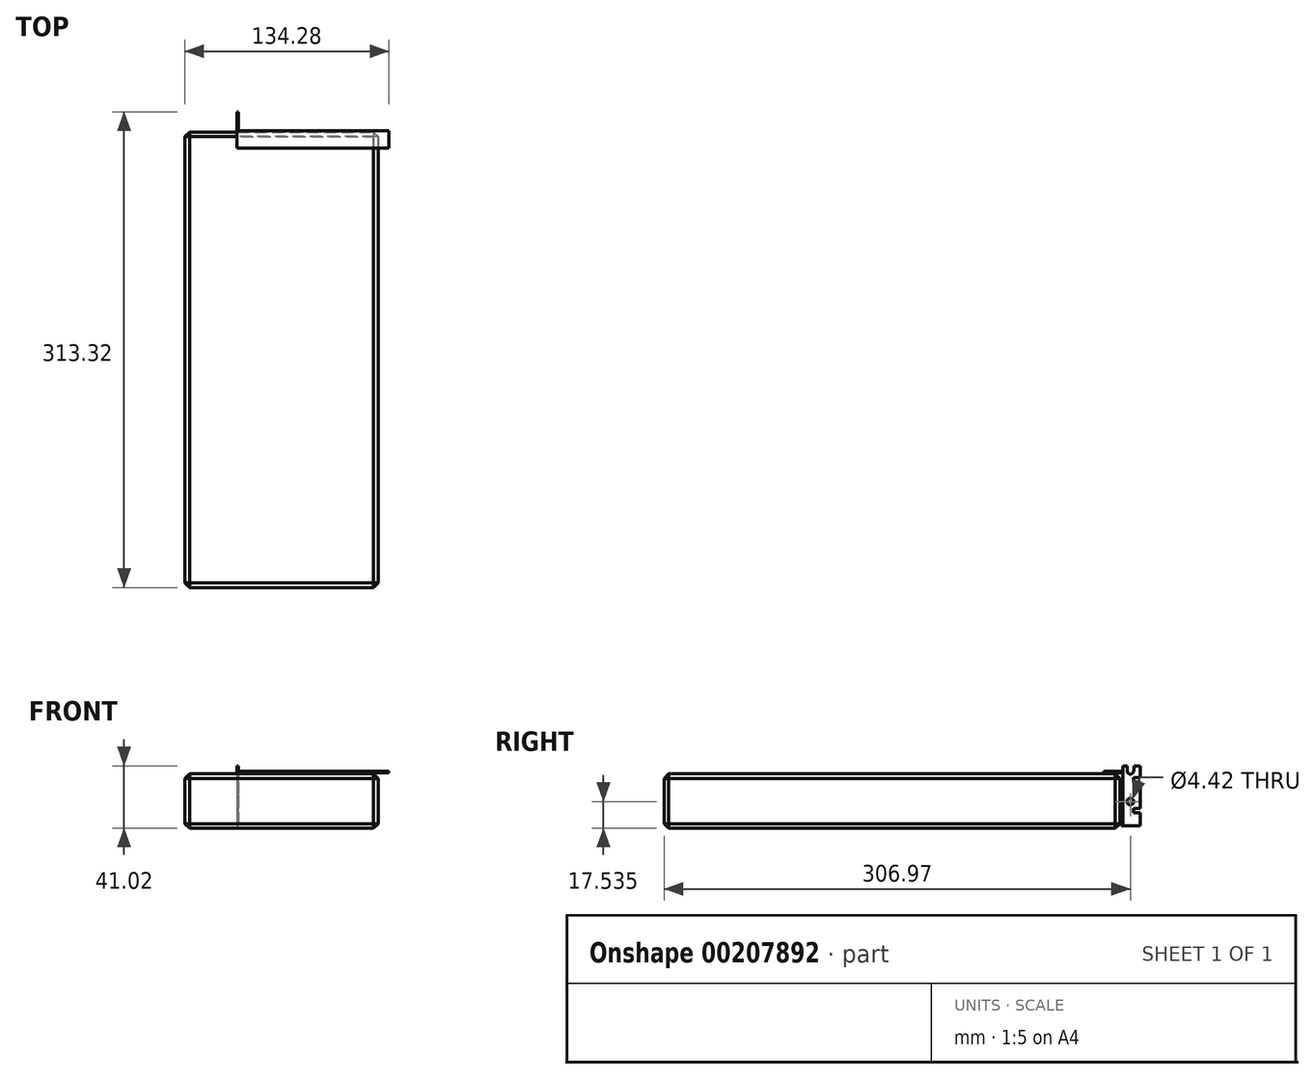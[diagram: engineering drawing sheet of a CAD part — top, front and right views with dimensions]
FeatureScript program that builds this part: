
annotation { "Feature Type Name" : "Feature", "Feature Type Description" : "" }
export const myFeature = defineFeature(function(context is Context, id is Id, definition is map)
    precondition{}
    {
        {
            var Q0;
            Q0=qCreatedBy(makeId("Top.planeOp"),FACE);
            var sketch = newSketch(context, id + "F0", { "sketchPlane" : qUnion([Q0])});
            skLineSegment(sketch, "E0.bottom", {"start": v(-143.4, -242.84) * mm, "end": v(-114.55, -242.84) * mm});
            skLineSegment(sketch, "E0.top", {"start": v(-143.4, 57.16) * mm, "end": v(-114.55, 57.16) * mm});
            skLineSegment(sketch, "E0.left", {"start": v(-143.4, -242.84) * mm, "end": v(-143.4, 57.16) * mm});
            skLineSegment(sketch, "E0.right", {"start": v(-114.55, -242.84) * mm, "end": v(-114.55, 57.16) * mm});
            skPoint(sketch, "E1", {"position": v(-3.4, -242.84) * mm});
            skLineSegment(sketch, "E2", {"start": v(11.76, 58.2) * mm, "end": v(11.76, 59.05) * mm});
            skLineSegment(sketch, "E3", {"start": v(11.76, 59.05) * mm, "end": v(-108.26, 59.05) * mm});
            skLineSegment(sketch, "E4", {"start": v(-108.26, 59.05) * mm, "end": v(-108.26, 70.48) * mm});
            skLineSegment(sketch, "E5", {"start": v(-108.26, 70.48) * mm, "end": v(-109.12, 70.48) * mm});
            skLineSegment(sketch, "E6.bottom", {"start": v(-114.55, -242.84) * mm, "end": v(-16.15, -242.84) * mm});
            skLineSegment(sketch, "E6.top", {"start": v(-114.55, 57.16) * mm, "end": v(-16.15, 57.16) * mm});
            skLineSegment(sketch, "E6.right", {"start": v(-16.15, -242.84) * mm, "end": v(-16.15, 57.16) * mm});
            skLineSegment(sketch, "E7.bottom", {"start": v(-16.15, 57.16) * mm, "end": v(-7.9, 57.16) * mm});
            skLineSegment(sketch, "E7.top", {"start": v(-16.15, 42.16) * mm, "end": v(-7.9, 42.16) * mm});
            skLineSegment(sketch, "E7.left", {"start": v(-16.15, 57.16) * mm, "end": v(-16.15, 42.16) * mm});
            skLineSegment(sketch, "E7.right", {"start": v(-7.9, 57.16) * mm, "end": v(-7.9, 42.16) * mm});
            skPoint(sketch, "E8", {"position": v(-7.9, -242.84) * mm});
            skLineSegment(sketch, "E9.bottom", {"start": v(-16.15, 23.8) * mm, "end": v(-7.9, 23.8) * mm});
            skLineSegment(sketch, "E9.top", {"start": v(-16.15, 15.8) * mm, "end": v(-7.9, 15.8) * mm});
            skLineSegment(sketch, "E9.left", {"start": v(-16.15, 23.8) * mm, "end": v(-16.15, 15.8) * mm});
            skLineSegment(sketch, "E9.right", {"start": v(-7.9, 23.8) * mm, "end": v(-7.9, 15.8) * mm});
            skPoint(sketch, "E10", {"position": v(-3.4, 57.16) * mm});
            skLineSegment(sketch, "E11", {"start": v(-16.15, 12.15) * mm, "end": v(-3.4, 12.15) * mm});
            skLineSegment(sketch, "E12", {"start": v(-3.4, 12.15) * mm, "end": v(-3.4, 0.95) * mm});
            skLineSegment(sketch, "E13", {"start": v(-3.4, 0.95) * mm, "end": v(-11.8, 0.95) * mm});
            skLineSegment(sketch, "E14", {"start": v(-11.8, 0.95) * mm, "end": v(-11.8, -0.95) * mm});
            skLineSegment(sketch, "E15", {"start": v(-11.8, -0.95) * mm, "end": v(-3.4, -0.95) * mm});
            skLineSegment(sketch, "E16", {"start": v(-3.4, -0.95) * mm, "end": v(-3.4, -72.15) * mm});
            skLineSegment(sketch, "E17", {"start": v(-3.4, -72.15) * mm, "end": v(-16.15, -72.15) * mm});
            skPoint(sketch, "E18", {"position": v(-11.8, 0) * mm});
            skArc(sketch, "E19", {"start": v(-14.32, 15.8) * mm, "mid": v(-16.15, 13.98) * mm, "end": v(-14.32, 12.15) * mm});
            skArc(sketch, "E20", {"start": v(-10.85, 0.95) * mm, "mid": v(-11.8, 0) * mm, "end": v(-10.85, -0.95) * mm});
            skLineSegment(sketch, "E21", {"start": v(-16.15, -81.9) * mm, "end": v(-11.35, -81.9) * mm});
            skLineSegment(sketch, "E22", {"start": v(-11.35, -81.9) * mm, "end": v(-11.35, -87.6) * mm});
            skLineSegment(sketch, "E23", {"start": v(-11.35, -87.6) * mm, "end": v(-8.77, -87.6) * mm});
            skLineSegment(sketch, "E24", {"start": v(-8.77, -87.6) * mm, "end": v(-6.35, -86.2) * mm});
            skLineSegment(sketch, "E25", {"start": v(-6.35, -86.2) * mm, "end": v(-6.35, -74.9) * mm});
            skLineSegment(sketch, "E26", {"start": v(-6.35, -74.9) * mm, "end": v(-12.38, -74.9) * mm});
            skLineSegment(sketch, "E27", {"start": v(-12.38, -74.9) * mm, "end": v(-12.38, -72.15) * mm});
            skArc(sketch, "E28", {"start": v(-11, -72.15) * mm, "mid": v(-12.38, -73.53) * mm, "end": v(-11, -74.9) * mm});
            skLineSegment(sketch, "E29", {"start": v(-108.26, 59.05) * mm, "end": v(-109.12, 59.05) * mm});
            skLineSegment(sketch, "E30", {"start": v(-109.12, 70.48) * mm, "end": v(-109.12, 59.05) * mm});
            skLineSegment(sketch, "E31", {"start": v(-109.12, 58.2) * mm, "end": v(-109.12, 59.05) * mm});
            skLineSegment(sketch, "E32", {"start": v(-108.26, 59.05) * mm, "end": v(-108.26, 58.2) * mm});
            skLineSegment(sketch, "E33", {"start": v(-108.26, 58.2) * mm, "end": v(-109.12, 58.2) * mm});
            skLineSegment(sketch, "E34", {"start": v(-108.26, 58.2) * mm, "end": v(11.76, 58.2) * mm});
            skPoint(sketch, "E35", {"position": v(0, 0) * mm});
            skPoint(sketch, "E36", {"position": v(0, 57.16) * mm});
            skSolve(sketch);
        }
        {
            var Q0;
            {var subQ7=sQuery(id+"F0.wireOp",EDGE,"E6.bottom");Q0=makeQuery(id+"F0.imprint","IMPRINT",FACE,{"disambiguationData":[TD([[makeQuery(id+"F0.imprint","IMPRINT",EDGE,{"derivedFrom":subQ7}),1.0]])]});}
            var Q1;
            Q1=makeQuery(id+"F0.imprint","IMPRINT",FACE,{"disambiguationData":[TD([[makeQuery(id+"F0.imprint","IMPRINT",EDGE,{"derivedFrom":sQuery(id+"F0.wireOp",EDGE,"E0.bottom")}),1.0]])]});
            var Q2;
            {var subQ5=sQuery(id+"F0.wireOp",EDGE,"E21");Q2=makeQuery(id+"F0.imprint","IMPRINT",FACE,{"disambiguationData":[TD([[makeQuery(id+"F0.imprint","IMPRINT",EDGE,{"derivedFrom":subQ5}),1.0]])]});}
            var Q3;
            {var subQ0=sQuery(id+"F0.wireOp",EDGE,"E27");var subQ1=sQuery(id+"F0.wireOp",EDGE,"E26");var subQ2=makeQuery(id+"F0.imprint","INTERSECT",VERTEX,{"derivedFrom":[subQ1,subQ0]});Q3=makeQuery(id+"F0.imprint","IMPRINT",FACE,{"disambiguationData":[TD([[makeQuery(id+"F0.imprint","IMPRINT",EDGE,{"disambiguationData":[TD([[subQ2,1.0]])],"derivedFrom":subQ1}),-1.0]])]});}
            var Q4;
            {var subQ0=sQuery(id+"F0.wireOp",EDGE,"E27");var subQ1=sQuery(id+"F0.wireOp",EDGE,"E17");var subQ2=makeQuery(id+"F0.imprint","INTERSECT",VERTEX,{"derivedFrom":[subQ1,subQ0]});Q4=makeQuery(id+"F0.imprint","IMPRINT",FACE,{"disambiguationData":[TD([[makeQuery(id+"F0.imprint","IMPRINT",EDGE,{"disambiguationData":[TD([[subQ2,1.0]])],"derivedFrom":subQ1}),1.0]])]});}
            var Q5;
            {var subQ0=sQuery(id+"F0.wireOp",EDGE,"E15");var subQ1=sQuery(id+"F0.wireOp",EDGE,"E14");var subQ2=makeQuery(id+"F0.imprint","INTERSECT",VERTEX,{"derivedFrom":[subQ1,subQ0]});Q5=makeQuery(id+"F0.imprint","IMPRINT",FACE,{"disambiguationData":[TD([[makeQuery(id+"F0.imprint","IMPRINT",EDGE,{"disambiguationData":[TD([[subQ2,1.0]])],"derivedFrom":subQ1}),1.0]])]});}
            var Q6;
            {var subQ0=sQuery(id+"F0.wireOp",EDGE,"E14");var subQ1=sQuery(id+"F0.wireOp",EDGE,"E13");var subQ2=makeQuery(id+"F0.imprint","INTERSECT",VERTEX,{"derivedFrom":[subQ1,subQ0]});Q6=makeQuery(id+"F0.imprint","IMPRINT",FACE,{"disambiguationData":[TD([[makeQuery(id+"F0.imprint","IMPRINT",EDGE,{"disambiguationData":[TD([[subQ2,1.0]])],"derivedFrom":subQ1}),1.0]])]});}
            var Q7;
            {var subQ7=sQuery(id+"F0.wireOp",EDGE,"E12");Q7=makeQuery(id+"F0.imprint","IMPRINT",FACE,{"disambiguationData":[TD([[makeQuery(id+"F0.imprint","IMPRINT",EDGE,{"derivedFrom":subQ7}),-1.0]])]});}
            var Q8;
            {var subQ0=sQuery(id+"F0.wireOp",EDGE,"E11");var subQ1=sQuery(id+"F0.wireOp",EDGE,"E6.right");var subQ2=makeQuery(id+"F0.imprint","INTERSECT",VERTEX,{"derivedFrom":[subQ1,subQ0]});Q8=makeQuery(id+"F0.imprint","IMPRINT",FACE,{"disambiguationData":[TD([[makeQuery(id+"F0.imprint","IMPRINT",EDGE,{"disambiguationData":[TD([[subQ2,-1.0]])],"derivedFrom":subQ1}),-1.0]])]});}
            var Q9;
            {var subQ0=sQuery(id+"F0.wireOp",EDGE,"E9.top");var subQ3=sQuery(id+"F0.wireOp",EDGE,"E19");var subQ5=makeQuery(id+"F0.imprint","INTERSECT",VERTEX,{"derivedFrom":[subQ0,subQ3]});Q9=makeQuery(id+"F0.imprint","IMPRINT",FACE,{"disambiguationData":[TD([[makeQuery(id+"F0.imprint","IMPRINT",EDGE,{"disambiguationData":[TD([[subQ5,-1.0]])],"derivedFrom":subQ3}),-1.0]])]});}
            var Q10;
            Q10=makeQuery(id+"F0.imprint","IMPRINT",FACE,{"disambiguationData":[TD([[makeQuery(id+"F0.imprint","IMPRINT",EDGE,{"derivedFrom":sQuery(id+"F0.wireOp",EDGE,"E9.bottom")}),-1.0]])]});
            var Q11;
            Q11=makeQuery(id+"F0.imprint","IMPRINT",FACE,{"disambiguationData":[TD([[makeQuery(id+"F0.imprint","IMPRINT",EDGE,{"derivedFrom":sQuery(id+"F0.wireOp",EDGE,"E7.bottom")}),-1.0]])]});
            extrude(context, id + "F1", {"entities" : qUnion([Q0, Q1, Q2, Q3, Q4, Q5, Q6, Q7, Q8, Q9, Q10, Q11]), "endBound" : BoundingType.SYMMETRIC, "depth" : 1.57 * mm});
        }
        {
            var Q0;
            Q0=makeQuery(id+"F0.imprint","IMPRINT",FACE,{"disambiguationData":[TD([[makeQuery(id+"F0.imprint","IMPRINT",EDGE,{"derivedFrom":sQuery(id+"F0.wireOp",EDGE,"E2")}),1.0]])]});
            extrude(context, id + "F2", {"entities" : qUnion([Q0]), "depth" : 10 * mm, "hasSecondDirection" : true, "secondDirectionOppositeDirection" : true, "secondDirectionDepth" : 40 * mm});
        }
        {
            var Q0;
            Q0=makeQuery(id+"F2.opExtrude","SWEPT_FACE",FACE,{"disambiguationData":[OSD([sQuery(id+"F0.wireOp",EDGE,"E3")])]});
            var sketch = newSketch(context, id + "F3", { "sketchPlane" : qUnion([Q0])});
            skLineSegment(sketch, "E37", {"start": v(-4.49, -2.06) * mm, "end": v(-11.76, -2.06) * mm});
            skLineSegment(sketch, "E38", {"start": v(-11.76, -2.06) * mm, "end": v(-11.76, -12.25) * mm});
            skLineSegment(sketch, "E39", {"start": v(-11.76, -12.25) * mm, "end": v(-4.49, -12.25) * mm});
            skLineSegment(sketch, "E40", {"start": v(-4.49, -12.25) * mm, "end": v(-0.38, -16.37) * mm});
            skLineSegment(sketch, "E41", {"start": v(-0.38, -16.36) * mm, "end": v(101.78, -16.36) * mm});
            skLineSegment(sketch, "E42", {"start": v(108.26, -13.82) * mm, "end": v(108.26, 5.23) * mm});
            skLineSegment(sketch, "E43", {"start": v(108.26, 5.23) * mm, "end": v(105.34, 5.23) * mm});
            skLineSegment(sketch, "E44", {"start": v(103.7, 2.06) * mm, "end": v(-0.37, 2.05) * mm});
            skLineSegment(sketch, "E45", {"start": v(-0.37, 2.05) * mm, "end": v(-4.49, -2.06) * mm});
            skLineSegment(sketch, "E46.bottom", {"start": v(7.9, 0.79) * mm, "end": v(114.55, 0.79) * mm});
            skLineSegment(sketch, "E46.top", {"start": v(7.9, -0.78) * mm, "end": v(114.55, -0.78) * mm});
            skLineSegment(sketch, "E46.left", {"start": v(7.9, 0.78) * mm, "end": v(7.9, -0.78) * mm});
            skLineSegment(sketch, "E46.right", {"start": v(114.55, 0.79) * mm, "end": v(114.55, -0.78) * mm});
            skPoint(sketch, "E47", {"position": v(7.9, 0) * mm});
            skLineSegment(sketch, "E48", {"start": v(108.26, -13.82) * mm, "end": v(104.32, -13.82) * mm});
            skLineSegment(sketch, "E49", {"start": v(104.32, -13.82) * mm, "end": v(101.78, -16.36) * mm});
            skLineSegment(sketch, "E50", {"start": v(103.7, 2.05) * mm, "end": v(103.7, 3.59) * mm});
            skLineSegment(sketch, "E51", {"start": v(103.7, 3.59) * mm, "end": v(105.34, 5.23) * mm});
            skPoint(sketch, "E52", {"position": v(0, 0) * mm});
            skLineSegment(sketch, "E53", {"start": v(-11.76, -22.39) * mm, "end": v(-11.76, -32.58) * mm});
            skLineSegment(sketch, "E54", {"start": v(-11.76, -32.57) * mm, "end": v(-4.49, -32.57) * mm});
            skLineSegment(sketch, "E55", {"start": v(-4.49, -32.57) * mm, "end": v(-0.38, -36.69) * mm});
            skLineSegment(sketch, "E56", {"start": v(-0.38, -36.69) * mm, "end": v(101.78, -36.68) * mm});
            skLineSegment(sketch, "E57", {"start": v(104.32, -34.14) * mm, "end": v(101.78, -36.68) * mm});
            skLineSegment(sketch, "E58", {"start": v(104.32, -34.14) * mm, "end": v(108.26, -34.14) * mm});
            skLineSegment(sketch, "E59", {"start": v(108.26, -34.14) * mm, "end": v(108.26, -15.1) * mm});
            skLineSegment(sketch, "E60", {"start": v(108.26, -15.1) * mm, "end": v(105.34, -15.1) * mm});
            skLineSegment(sketch, "E61", {"start": v(105.34, -15.1) * mm, "end": v(103.7, -16.73) * mm});
            skLineSegment(sketch, "E62", {"start": v(103.7, -16.73) * mm, "end": v(103.7, -18.26) * mm});
            skLineSegment(sketch, "E63", {"start": v(103.7, -18.26) * mm, "end": v(-0.37, -18.27) * mm});
            skLineSegment(sketch, "E64", {"start": v(-11.76, -22.39) * mm, "end": v(-4.49, -22.39) * mm});
            skLineSegment(sketch, "E65", {"start": v(-4.49, -22.39) * mm, "end": v(-0.37, -18.27) * mm});
            skLineSegment(sketch, "E66", {"start": v(-0.38, -16.37) * mm, "end": v(-0.37, -18.27) * mm});
            skLineSegment(sketch, "E67", {"start": v(108.26, -13.82) * mm, "end": v(108.26, -15.1) * mm});
            skSolve(sketch);
        }
        {
            var Q0;
            Q0=qSketchRegion(id+"F3",true);
            extrude(context, id + "F4", {"entities" : qUnion([Q0]), "operationType" : NewBodyOperationType.INTERSECT, "oppositeDirection" : true, "depth" : 5 * mm});
        }
        {
            var Q0;
            Q0=makeQuery(id+"F0.imprint","IMPRINT",FACE,{"disambiguationData":[TD([[makeQuery(id+"F0.imprint","IMPRINT",EDGE,{"derivedFrom":sQuery(id+"F0.wireOp",EDGE,"E29")}),1.0]])]});
            var Q1;
            Q1=makeQuery(id+"F0.imprint","IMPRINT",FACE,{"disambiguationData":[TD([[makeQuery(id+"F0.imprint","IMPRINT",EDGE,{"derivedFrom":sQuery(id+"F0.wireOp",EDGE,"E4")}),1.0]])]});
            extrude(context, id + "F5", {"entities" : qUnion([Q0, Q1]), "depth" : 10 * mm, "hasSecondDirection" : true, "secondDirectionOppositeDirection" : true, "secondDirectionDepth" : 40 * mm});
        }
        {
            var Q0;
            Q0=makeQuery(id+"F5.opExtrude","SWEPT_FACE",FACE,{"disambiguationData":[OSD([sQuery(id+"F0.wireOp",EDGE,"E30"),sQuery(id+"F0.wireOp",EDGE,"E31")])]});
            var sketch = newSketch(context, id + "F6", { "sketchPlane" : qUnion([Q0])});
            skLineSegment(sketch, "E68", {"start": v(-70.48, 5.23) * mm, "end": v(-70.48, -2.4) * mm});
            skLineSegment(sketch, "E69", {"start": v(-70.48, -2.4) * mm, "end": v(-66.29, -2.4) * mm});
            skLineSegment(sketch, "E70", {"start": v(-66.3, -2.4) * mm, "end": v(-66.3, -5.44) * mm});
            skLineSegment(sketch, "E71", {"start": v(-66.3, -5.44) * mm, "end": v(-70.48, -5.44) * mm});
            skLineSegment(sketch, "E72", {"start": v(-70.48, -5.44) * mm, "end": v(-70.48, -13.83) * mm});
            skLineSegment(sketch, "E73", {"start": v(-58.19, -13.83) * mm, "end": v(-58.19, 5.22) * mm});
            skLineSegment(sketch, "E74", {"start": v(-61.92, 5.22) * mm, "end": v(-61.92, -0.16) * mm});
            skLineSegment(sketch, "E75", {"start": v(-61.92, -0.15) * mm, "end": v(-66.34, -0.16) * mm});
            skLineSegment(sketch, "E76", {"start": v(-66.34, -0.16) * mm, "end": v(-66.34, 5.23) * mm});
            skLineSegment(sketch, "E77", {"start": v(-66.34, 5.23) * mm, "end": v(-70.48, 5.23) * mm});
            skPoint(sketch, "E78", {"position": v(-70.48, -16.37) * mm});
            skArc(sketch, "E79", {"start": v(-66.34, 2.06) * mm, "mid": v(-64.13, -0.16) * mm, "end": v(-61.92, 2.06) * mm});
            skLineSegment(sketch, "E80.bottom", {"start": v(-57.16, 0.79) * mm, "end": v(0, 0.79) * mm});
            skLineSegment(sketch, "E80.top", {"start": v(-57.16, -0.79) * mm, "end": v(0, -0.79) * mm});
            skLineSegment(sketch, "E80.left", {"start": v(-57.16, 0.79) * mm, "end": v(-57.16, -0.79) * mm});
            skPoint(sketch, "E81", {"position": v(-57.16, 0) * mm});
            skLineSegment(sketch, "E82.bottom", {"start": v(-46.48, 1.65) * mm, "end": v(-58.19, 1.65) * mm});
            skLineSegment(sketch, "E82.top", {"start": v(-46.48, 0.78) * mm, "end": v(-58.19, 0.78) * mm});
            skLineSegment(sketch, "E82.left", {"start": v(-46.48, 1.65) * mm, "end": v(-46.48, 0.78) * mm});
            skLineSegment(sketch, "E82.right", {"start": v(-58.19, 1.65) * mm, "end": v(-58.19, 0.78) * mm});
            skLineSegment(sketch, "E83", {"start": v(-59.05, 5.22) * mm, "end": v(-59.05, -13.83) * mm});
            skLineSegment(sketch, "E84", {"start": v(-61.92, 5.22) * mm, "end": v(-59.05, 5.22) * mm});
            skLineSegment(sketch, "E85", {"start": v(-59.05, 5.22) * mm, "end": v(-58.19, 5.22) * mm});
            skPoint(sketch, "E86", {"position": v(0, 0) * mm});
            skLineSegment(sketch, "E87", {"start": v(-59.05, -15.1) * mm, "end": v(-70.48, -15.1) * mm});
            skLineSegment(sketch, "E88", {"start": v(-70.48, -15.1) * mm, "end": v(-70.48, -22.71) * mm});
            skLineSegment(sketch, "E89", {"start": v(-70.48, -22.71) * mm, "end": v(-66.3, -22.71) * mm});
            skLineSegment(sketch, "E90", {"start": v(-66.3, -22.71) * mm, "end": v(-66.3, -25.76) * mm});
            skLineSegment(sketch, "E91", {"start": v(-66.3, -25.76) * mm, "end": v(-70.48, -25.76) * mm});
            skLineSegment(sketch, "E92", {"start": v(-70.48, -25.76) * mm, "end": v(-70.48, -34.14) * mm});
            skLineSegment(sketch, "E93", {"start": v(-70.48, -34.14) * mm, "end": v(-59.05, -34.14) * mm});
            skLineSegment(sketch, "E94", {"start": v(-59.05, -34.14) * mm, "end": v(-59.05, -15.1) * mm});
            skLineSegment(sketch, "E95.bottom", {"start": v(-59.05, -15.1) * mm, "end": v(-58.19, -15.1) * mm});
            skLineSegment(sketch, "E95.top", {"start": v(-59.05, -34.14) * mm, "end": v(-58.19, -34.14) * mm});
            skLineSegment(sketch, "E95.left", {"start": v(-59.05, -15.1) * mm, "end": v(-59.05, -34.14) * mm});
            skLineSegment(sketch, "E95.right", {"start": v(-58.19, -15.1) * mm, "end": v(-58.19, -34.14) * mm});
            skLineSegment(sketch, "E96", {"start": v(-59.05, -13.83) * mm, "end": v(-70.48, -13.83) * mm});
            skLineSegment(sketch, "E97", {"start": v(-59.05, -13.83) * mm, "end": v(-58.19, -13.83) * mm});
            skLineSegment(sketch, "E98.bottom", {"start": v(-70.48, -13.83) * mm, "end": v(-58.19, -13.83) * mm});
            skLineSegment(sketch, "E98.top", {"start": v(-70.48, -15.1) * mm, "end": v(-58.19, -15.1) * mm});
            skLineSegment(sketch, "E98.left", {"start": v(-70.48, -13.83) * mm, "end": v(-70.48, -15.1) * mm});
            skLineSegment(sketch, "E98.right", {"start": v(-58.19, -13.83) * mm, "end": v(-58.19, -15.1) * mm});
            skCircle(sketch, "E99", {"center": v(-64.13, -18.27) * mm, "radius": 2.2 * mm});
            skSolve(sketch);
        }
        {
            var Q0;
            {var subQ0=sQuery(id+"F6.wireOp",EDGE,"E76");var subQ1=sQuery(id+"F6.wireOp",EDGE,"E75");var subQ2=makeQuery(id+"F6.imprint","INTERSECT",VERTEX,{"derivedFrom":[subQ1,subQ0]});Q0=makeQuery(id+"F6.imprint","IMPRINT",FACE,{"disambiguationData":[TD([[makeQuery(id+"F6.imprint","IMPRINT",EDGE,{"disambiguationData":[TD([[subQ2,1.0]])],"derivedFrom":subQ1}),-1.0]])]});}
            var Q1;
            Q1=makeQuery(id+"F6.imprint","IMPRINT",FACE,{"disambiguationData":[TD([[makeQuery(id+"F6.imprint","IMPRINT",EDGE,{"derivedFrom":sQuery(id+"F6.wireOp",EDGE,"E68")}),1.0]])]});
            var Q2;
            {var subQ0=sQuery(id+"F6.wireOp",EDGE,"E75");var subQ1=sQuery(id+"F6.wireOp",EDGE,"E74");var subQ2=makeQuery(id+"F6.imprint","INTERSECT",VERTEX,{"derivedFrom":[subQ1,subQ0]});Q2=makeQuery(id+"F6.imprint","IMPRINT",FACE,{"disambiguationData":[TD([[makeQuery(id+"F6.imprint","IMPRINT",EDGE,{"disambiguationData":[TD([[subQ2,1.0]])],"derivedFrom":subQ1}),-1.0]])]});}
            var Q3;
            {var subQ3=sQuery(id+"F6.wireOp",EDGE,"E82.right");Q3=makeQuery(id+"F6.imprint","IMPRINT",FACE,{"disambiguationData":[TD([[makeQuery(id+"F6.imprint","IMPRINT",EDGE,{"derivedFrom":subQ3}),-1.0]])]});}
            var Q4;
            {var subQ0=sQuery(id+"F6.wireOp",EDGE,"E98.left");Q4=makeQuery(id+"F6.imprint","IMPRINT",FACE,{"disambiguationData":[TD([[makeQuery(id+"F6.imprint","IMPRINT",EDGE,{"derivedFrom":subQ0}),1.0]])]});}
            var Q5;
            {var subQ0=sQuery(id+"F6.wireOp",EDGE,"E88");Q5=makeQuery(id+"F6.imprint","IMPRINT",FACE,{"disambiguationData":[TD([[makeQuery(id+"F6.imprint","IMPRINT",EDGE,{"derivedFrom":subQ0}),1.0]])]});}
            var Q6;
            Q6=makeQuery(id+"F6.imprint","IMPRINT",FACE,{"disambiguationData":[TD([[makeQuery(id+"F6.imprint","IMPRINT",EDGE,{"derivedFrom":sQuery(id+"F6.wireOp",EDGE,"E95.top")}),1.0]])]});
            extrude(context, id + "F7", {"entities" : qUnion([Q0, Q1, Q2, Q3, Q4, Q5, Q6]), "operationType" : NewBodyOperationType.INTERSECT, "oppositeDirection" : true, "depth" : 1 * mm});
        }
        {
            var Q0;
            Q0=makeQuery(id+"F6.imprint","IMPRINT",FACE,{"disambiguationData":[TD([[makeQuery(id+"F6.imprint","IMPRINT",EDGE,{"derivedFrom":sQuery(id+"F6.wireOp",EDGE,"E82.bottom")}),1.0]])]});
            extrude(context, id + "F8", {"entities" : qUnion([Q0]), "oppositeDirection" : true, "depth" : 100 * mm});
        }
        {
            var Q0;
            {var subQ7=sQuery(id+"F0.wireOp",EDGE,"E6.bottom");Q0=makeQuery(id+"F0.imprint","IMPRINT",FACE,{"disambiguationData":[TD([[makeQuery(id+"F0.imprint","IMPRINT",EDGE,{"derivedFrom":subQ7}),1.0]])]});}
            var Q1;
            Q1=makeQuery(id+"F0.imprint","IMPRINT",FACE,{"disambiguationData":[TD([[makeQuery(id+"F0.imprint","IMPRINT",EDGE,{"derivedFrom":sQuery(id+"F0.wireOp",EDGE,"E0.bottom")}),1.0]])]});
            extrude(context, id + "F9", {"entities" : qUnion([Q0, Q1]), "oppositeDirection" : true, "depth" : 35.8 * mm});
        }
        {
            var Q0;
            Q0=makeQuery(id+"F9.opExtrude","CAP_EDGE",EDGE,{"disambiguationData":[OSD([sQuery(id+"F0.wireOp",EDGE,"E6.right"),sQuery(id+"F0.wireOp",EDGE,"E7.left"),sQuery(id+"F0.wireOp",EDGE,"E9.left")])],"isStart":false});
            var Q1;
            Q1=makeQuery(id+"F9.opExtrude","CAP_EDGE",EDGE,{"disambiguationData":[OSD([sQuery(id+"F0.wireOp",EDGE,"E0.left")])],"isStart":false});
            var Q2;
            Q2=makeQuery(id+"F9.opExtrude","CAP_EDGE",EDGE,{"disambiguationData":[OSD([sQuery(id+"F0.wireOp",EDGE,"E0.left")])],"isStart":true});
            var Q3;
            Q3=makeQuery(id+"F9.opExtrude","CAP_EDGE",EDGE,{"disambiguationData":[OSD([sQuery(id+"F0.wireOp",EDGE,"E6.right"),sQuery(id+"F0.wireOp",EDGE,"E7.left"),sQuery(id+"F0.wireOp",EDGE,"E9.left")])],"isStart":true});
            var Q4;
            Q4=makeQuery(id+"F9.opExtrude","CAP_EDGE",EDGE,{"disambiguationData":[OSD([sQuery(id+"F0.wireOp",EDGE,"E0.bottom"),sQuery(id+"F0.wireOp",EDGE,"E6.bottom")])],"isStart":true});
            var Q5;
            Q5=makeQuery(id+"F9.opExtrude","CAP_EDGE",EDGE,{"disambiguationData":[OSD([sQuery(id+"F0.wireOp",EDGE,"E0.bottom"),sQuery(id+"F0.wireOp",EDGE,"E6.bottom")])],"isStart":false});
            var Q6;
            Q6=makeQuery(id+"F9.opExtrude","CAP_EDGE",EDGE,{"disambiguationData":[OSD([sQuery(id+"F0.wireOp",EDGE,"E0.top"),sQuery(id+"F0.wireOp",EDGE,"E6.top")])],"isStart":false});
            var Q7;
            Q7=makeQuery(id+"F9.opExtrude","CAP_EDGE",EDGE,{"disambiguationData":[OSD([sQuery(id+"F0.wireOp",EDGE,"E0.top"),sQuery(id+"F0.wireOp",EDGE,"E6.top")])],"isStart":true});
            var Q8;
            Q8=makeQuery(id+"F9.opExtrude","SWEPT_EDGE",EDGE,{"disambiguationData":[OSD([sQuery(id+"F0.wireOp",EDGE,"E0.top"),sQuery(id+"F0.wireOp",EDGE,"E0.left")])]});
            var Q9;
            Q9=makeQuery(id+"F9.opExtrude","SWEPT_EDGE",EDGE,{"disambiguationData":[OSD([sQuery(id+"F0.wireOp",EDGE,"E6.top"),sQuery(id+"F0.wireOp",EDGE,"E7.bottom"),sQuery(id+"F0.wireOp",EDGE,"E7.left")])]});
            var Q10;
            Q10=makeQuery(id+"F9.opExtrude","SWEPT_EDGE",EDGE,{"disambiguationData":[OSD([sQuery(id+"F0.wireOp",EDGE,"E6.bottom"),sQuery(id+"F0.wireOp",EDGE,"E6.right")])]});
            var Q11;
            Q11=makeQuery(id+"F9.opExtrude","SWEPT_EDGE",EDGE,{"disambiguationData":[OSD([sQuery(id+"F0.wireOp",EDGE,"E0.bottom"),sQuery(id+"F0.wireOp",EDGE,"E0.left")])]});
            chamfer(context, id + "F10", {"entities" : qUnion([Q0, Q1, Q2, Q3, Q4, Q5, Q6, Q7, Q8, Q9, Q10, Q11]), "width" : 3 * mm, "tangentPropagation" : true});
        }
    });
